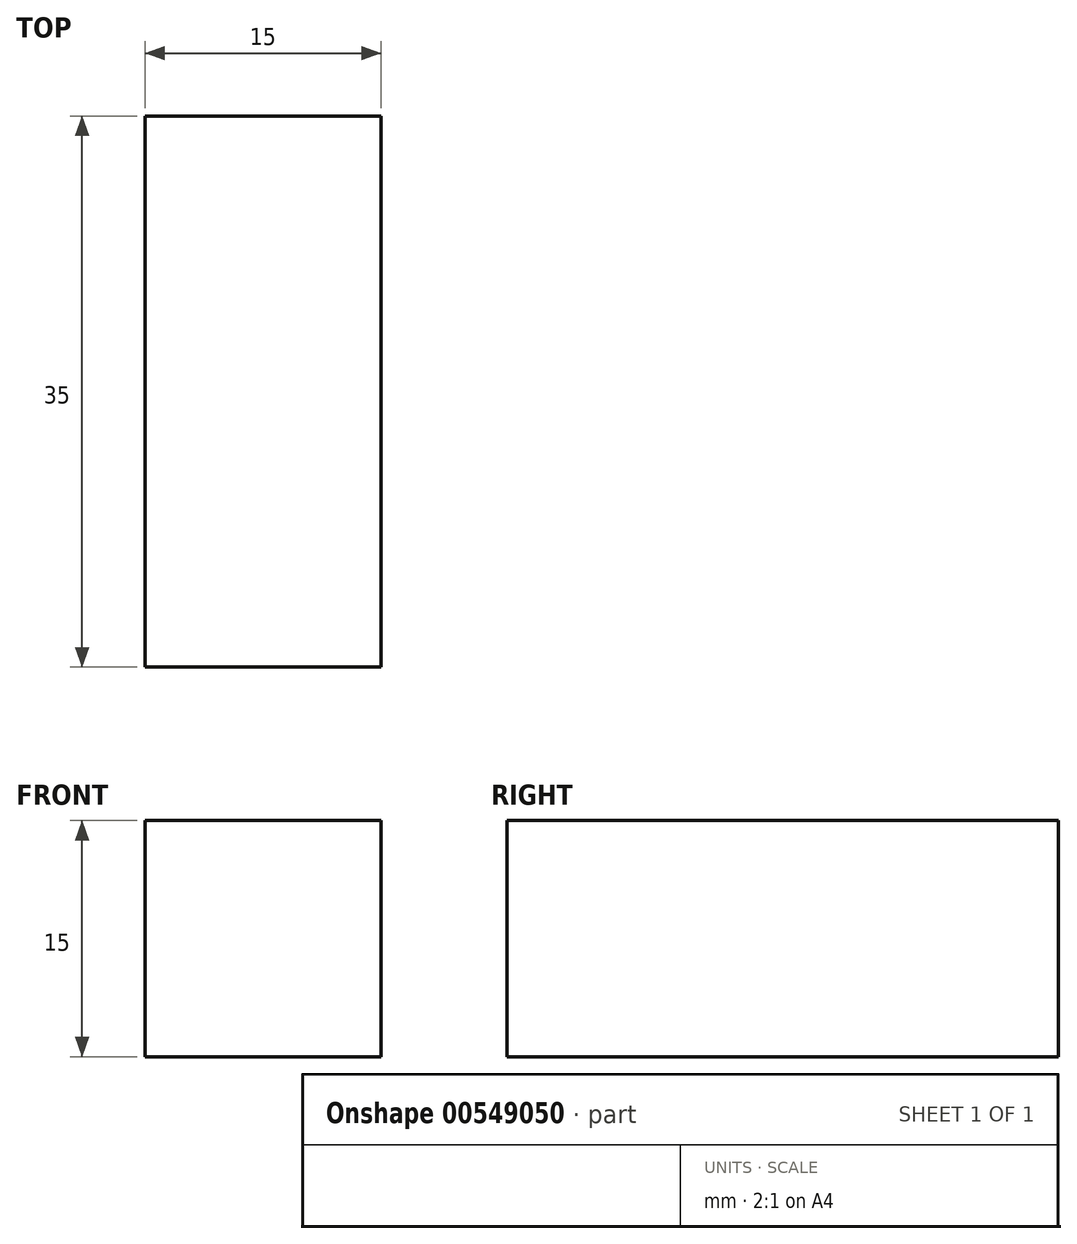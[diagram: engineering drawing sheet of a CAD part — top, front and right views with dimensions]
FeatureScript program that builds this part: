
annotation { "Feature Type Name" : "Feature", "Feature Type Description" : "" }
export const myFeature = defineFeature(function(context is Context, id is Id, definition is map)
    precondition{}
    {
        {
            var Q0;
            Q0=qCreatedBy(makeId("Top.planeOp"),FACE);
            var sketch = newSketch(context, id + "F0", { "sketchPlane" : qUnion([Q0])});
            skLineSegment(sketch, "E0.bottom", {"start": v(-60.2, 41.01) * mm, "end": v(-45.2, 41.01) * mm});
            skLineSegment(sketch, "E0.top", {"start": v(-60.2, 6.01) * mm, "end": v(-45.2, 6.01) * mm});
            skLineSegment(sketch, "E0.left", {"start": v(-60.2, 41.01) * mm, "end": v(-60.2, 6.01) * mm});
            skLineSegment(sketch, "E0.right", {"start": v(-45.2, 41.01) * mm, "end": v(-45.2, 6.01) * mm});
            skSolve(sketch);
        }
        {
            var Q0;
            Q0=makeQuery(id+"F0.imprint","IMPRINT",FACE,{"disambiguationData":[TD([[makeQuery(id+"F0.imprint","IMPRINT",EDGE,{"derivedFrom":sQuery(id+"F0.wireOp",EDGE,"E0.bottom")}),-1.0]])]});
            extrude(context, id + "F1", {"entities" : qUnion([Q0]), "endBound" : BoundingType.SYMMETRIC, "depth" : 15 * mm, "offsetDistance" : 25 * mm});
        }
    });
